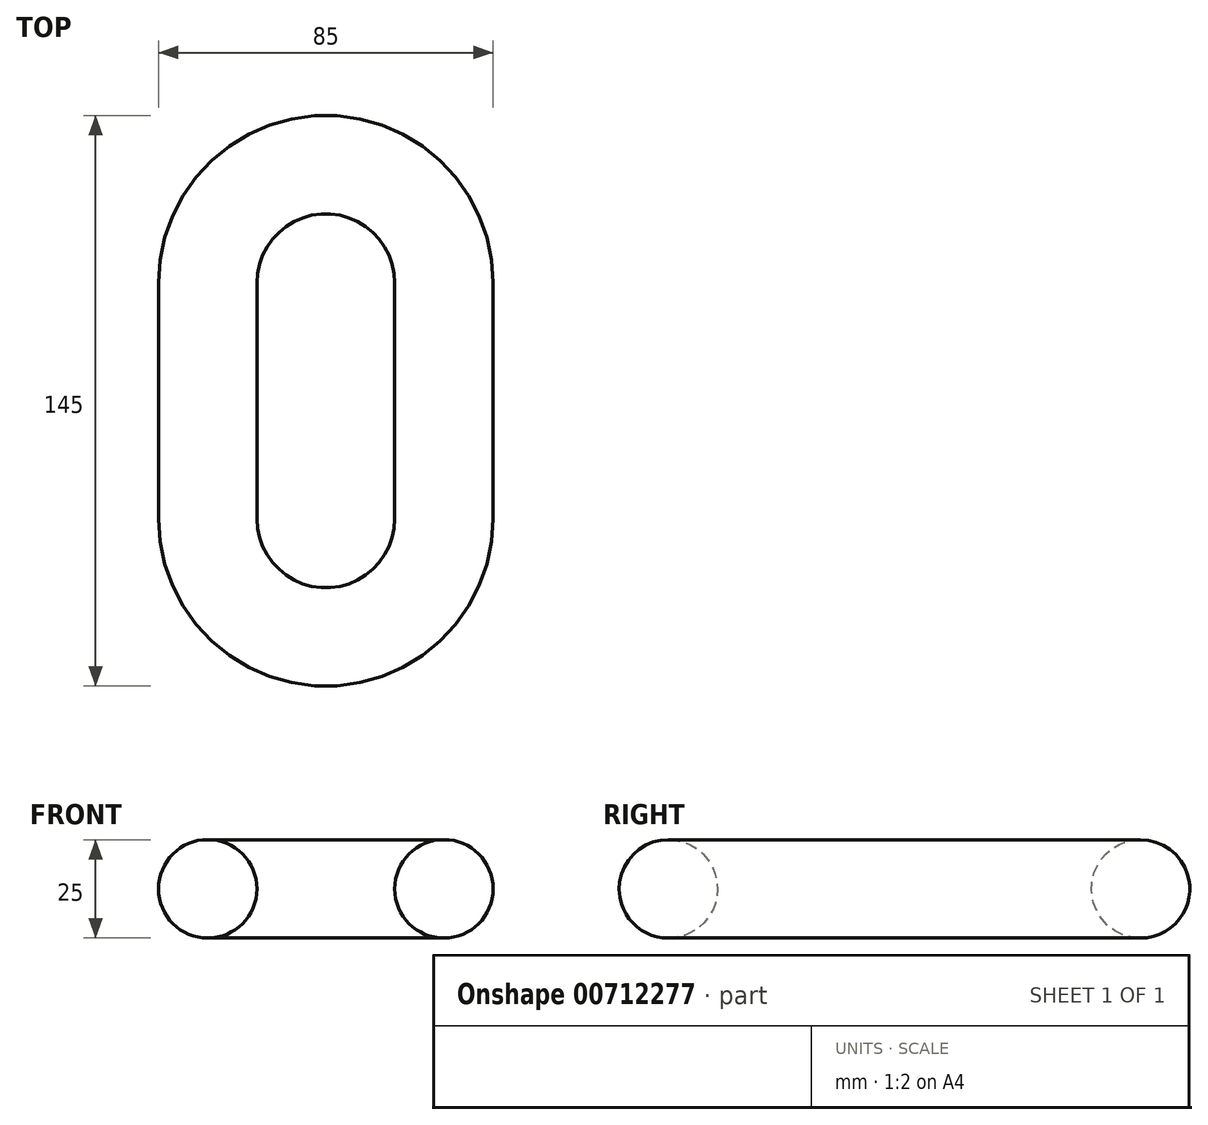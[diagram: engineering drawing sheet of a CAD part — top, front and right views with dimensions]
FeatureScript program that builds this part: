
annotation { "Feature Type Name" : "Feature", "Feature Type Description" : "" }
export const myFeature = defineFeature(function(context is Context, id is Id, definition is map)
    precondition{}
    {
        {
            var Q0;
            Q0=qCreatedBy(makeId("Front.planeOp"),FACE);
            var sketch = newSketch(context, id + "F0", { "sketchPlane" : qUnion([Q0])});
            skCircle(sketch, "E0", {"center": v(30, 0) * mm, "radius": 12.5 * mm});
            skLineSegment(sketch, "E1", {"start": v(0, 37.22) * mm, "end": v(0, -39.12) * mm});
            skSolve(sketch);
        }
        {
            var Q0;
            Q0=makeQuery(id+"F0.imprint","IMPRINT",FACE,{"disambiguationData":[TD([[makeQuery(id+"F0.imprint","IMPRINT",EDGE,{"derivedFrom":sQuery(id+"F0.wireOp",EDGE,"E0")}),1.0]])]});
            var Q1;
            Q1=sQuery(id+"F0.wireOp",EDGE,"E1");
            revolve(context, id + "F1", {"surfaceOperationType" : NewSurfaceOperationType.NEW, "entities" : qUnion([Q0]), "axis" : qUnion([Q1]), "revolveType" : RevolveType.ONE_DIRECTION, "oppositeDirection" : true, "angle" : 180 * degree});
        }
        {
            var Q0;
            Q0=makeQuery(id+"F1.opRevolve","CAP_FACE",FACE,{"disambiguationData":[OSD([sQuery(id+"F0.wireOp",EDGE,"E0")])],"isStart":true});
            var Q1;
            Q1=makeQuery(id+"F1.opRevolve","CAP_FACE",FACE,{"disambiguationData":[OSD([sQuery(id+"F0.wireOp",EDGE,"E0")])],"isStart":false});
            extrude(context, id + "F2", {"entities" : qUnion([Q0, Q1]), "operationType" : NewBodyOperationType.ADD, "depth" : 60 * mm, "offsetDistance" : 25 * mm});
        }
        {
            var Q0;
            {var subQ0=sQuery(id+"F0.wireOp",EDGE,"E0");Q0=makeQuery(id+"F2.opExtrude","CAP_FACE",FACE,{"disambiguationData":[OSD([subQ0]),TDD([makeQuery(id+"F1.opRevolve","CAP_FACE",FACE,{"disambiguationData":[OSD([subQ0])],"isStart":true})])],"isStart":false});}
            var sketch = newSketch(context, id + "F3", { "sketchPlane" : qUnion([Q0])});
            skCircle(sketch, "E2", {"center": v(30, 0) * mm, "radius": 12.5 * mm});
            skLineSegment(sketch, "E3", {"start": v(0, 24.79) * mm, "end": v(0, -42.35) * mm});
            skSolve(sketch);
        }
        {
            var Q0;
            Q0=makeQuery(id+"F3.imprint","IMPRINT",FACE,{"disambiguationData":[TD([[makeQuery(id+"F3.imprint","IMPRINT",EDGE,{"derivedFrom":sQuery(id+"F3.wireOp",EDGE,"E2")}),1.0]])]});
            var Q1;
            Q1=sQuery(id+"F3.wireOp",EDGE,"E3");
            revolve(context, id + "F4", {"operationType" : NewBodyOperationType.ADD, "surfaceOperationType" : NewSurfaceOperationType.NEW, "entities" : qUnion([Q0]), "axis" : qUnion([Q1]), "revolveType" : RevolveType.ONE_DIRECTION, "angle" : 180 * degree});
        }
    });
